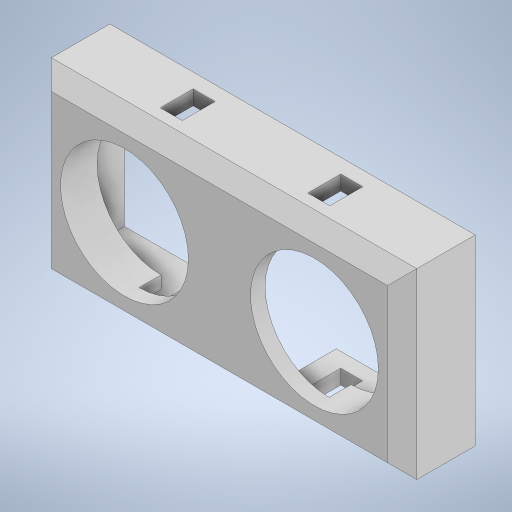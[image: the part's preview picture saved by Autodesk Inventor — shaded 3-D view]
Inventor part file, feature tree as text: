
AUTODESK INVENTOR PART (.ipt)
format: ipt  version: 2024.2 (Build 282272000, 272)  size: 305,152 bytes
history: native  units: mm
features: extrude x4, sketch x4, chamfer x1
ambient origin geometry x8: Origin, YZ Plane, XZ Plane, XY Plane, X Axis, Y Axis, Z Axis, Center Point
bodies: Solid1 (feature_tree)
feature tree (9):
  extrude  "Extrusion1"  Depth=17.5mm
  extrude  "Extrusion2"  Depth=50.0mm
  extrude  "Extrusion3"  Depth=12.0mm
  chamfer  "Chamfer2"  Distance=2.0mm
  extrude  "Extrusion4"  Depth=2.0mm
  sketch  "Sketch1"  dims[d0=17.5mm d1=17.5mm]
  sketch  "Sketch2"  dims[d2=26.0mm d3=50.0mm]
  sketch  "Sketch3"  dims[d4=25.0mm d5=12.0mm]
  sketch  "Sketch5"  dims[d6=12.5mm d7=2.0mm d8=0.0mm d12=2.0mm d14=46.0mm d15=2.0mm d16=21.0mm d17=8.0mm d18=0.0mm d19=12.0mm d20=19.0mm d21=2.0mm d22=2.0mm d23=25.0mm d24=3.0mm d25=0.0mm d26=2.0mm d27=2.0mm d28=45.0deg d29=3.0mm d31=3.0mm d33=17.2mm d34=13.4mm d35=1.5mm d36=3.0mm d37=0.0mm d38=2.0mm d39=1.5mm]
